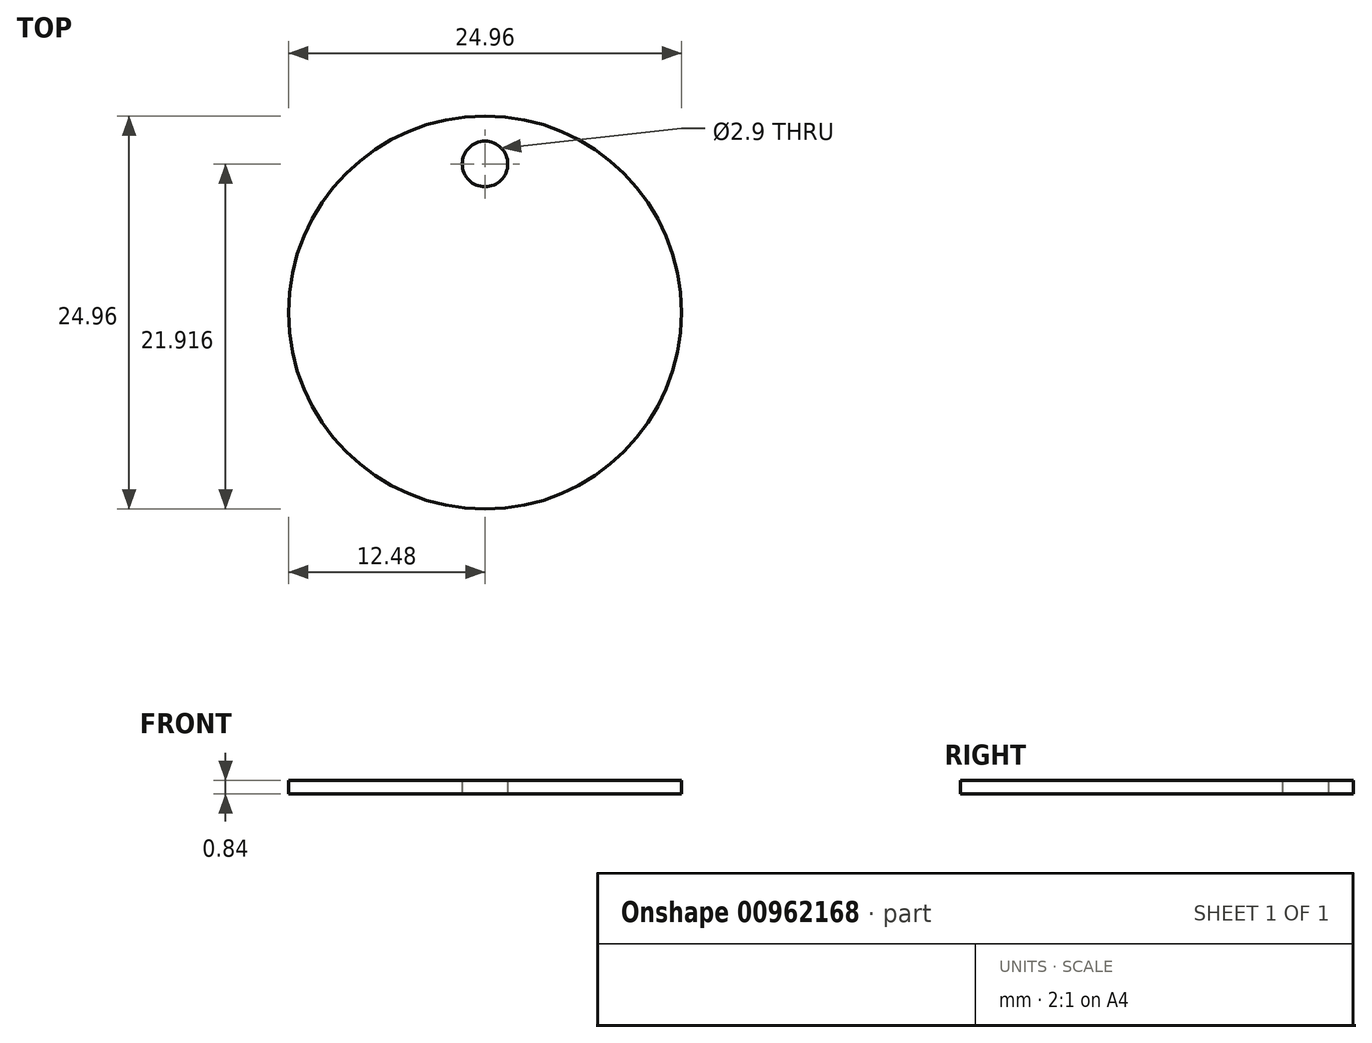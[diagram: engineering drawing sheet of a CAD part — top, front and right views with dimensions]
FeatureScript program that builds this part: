
annotation { "Feature Type Name" : "Feature", "Feature Type Description" : "" }
export const myFeature = defineFeature(function(context is Context, id is Id, definition is map)
    precondition{}
    {
        {
            var Q0;
            Q0=qCreatedBy(makeId("Top.planeOp"),FACE);
            var sketch = newSketch(context, id + "F0", { "sketchPlane" : qUnion([Q0])});
            skCircle(sketch, "E0", {"center": v(0, 0) * mm, "radius": 12.48 * mm});
            skCircle(sketch, "E1", {"center": v(0, 9.44) * mm, "radius": 1.45 * mm});
            skSolve(sketch);
        }
        {
            var Q0;
            Q0=makeQuery(id+"F0.imprint","IMPRINT",FACE,{"disambiguationData":[TD([[makeQuery(id+"F0.imprint","IMPRINT",EDGE,{"derivedFrom":sQuery(id+"F0.wireOp",EDGE,"E0")}),1.0]])]});
            extrude(context, id + "F1", {"entities" : qUnion([Q0]), "depth" : 0.84 * mm, "offsetDistance" : 25.4 * mm});
        }
    });
